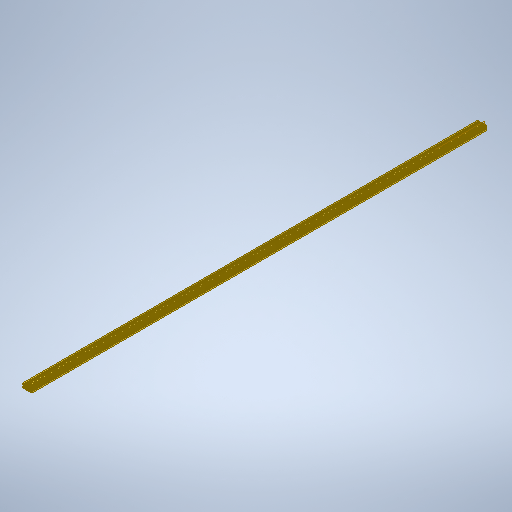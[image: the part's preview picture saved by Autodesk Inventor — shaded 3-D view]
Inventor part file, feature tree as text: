
AUTODESK INVENTOR PART (.ipt)
format: ipt  version: 2025.2 (Build 292293000, 293)  size: 441,856 bytes
history: native  units: mm
features: other x2, mirror x2, fillet x2, extrude x1, sketch x1
ambient origin geometry x8: Origin, YZ Plane, XZ Plane, XY Plane, X Axis, Y Axis, Z Axis, Center Point
bodies: Body1 (feature_tree)
feature tree (8):
  other  "Sólido1"
  extrude  "Extrusão1"  Depth=6.2mm
  mirror  "Espelhar3"
  mirror  "Espelhar4"
  fillet  "Arredondamento1"  Radius=5.0mm
  fillet  "Arredondamento2"  Radius=10.0mm
  other  "Plano de trabalho1"
  sketch  "Esboço1"  dims[d0=40.0mm d1=6.2mm d3=5.0mm d6=10.0mm d7=6.0mm d8=20.0mm d11=2.0mm d12=2000.0mm d13=0.0mm d15=0.5mm d18=6.0mm d19=0.5mm d21=4.0mm d22=1.0mm d23=1.0mm]
